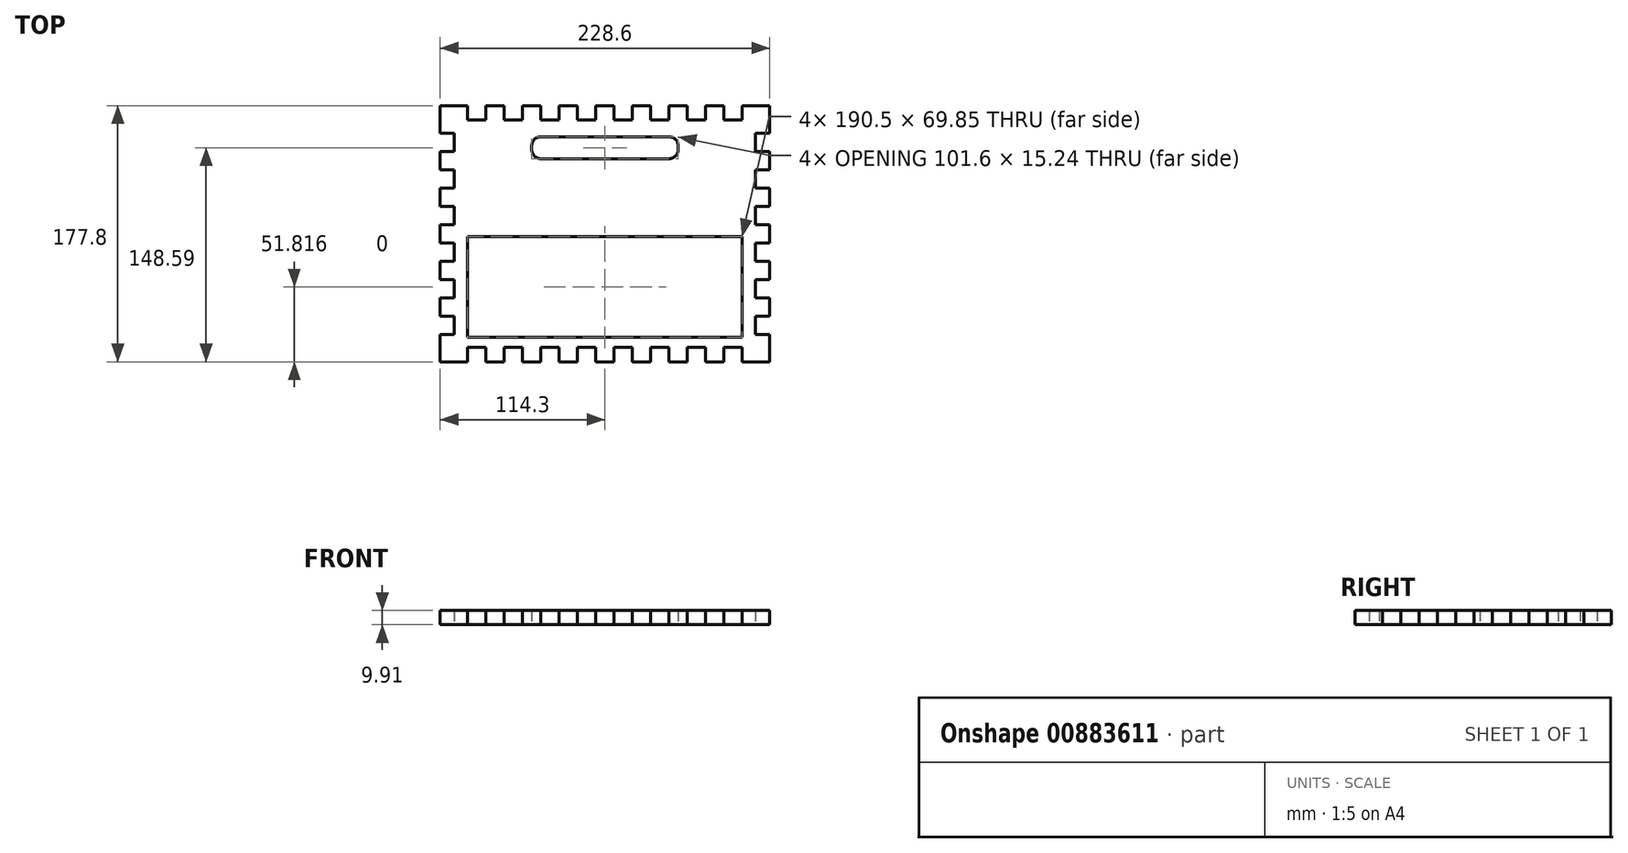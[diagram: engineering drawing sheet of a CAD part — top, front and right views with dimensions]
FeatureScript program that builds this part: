
annotation { "Feature Type Name" : "Feature", "Feature Type Description" : "" }
export const myFeature = defineFeature(function(context is Context, id is Id, definition is map)
    precondition{}
    {
        {
            var Q0;
            Q0=qCreatedBy(makeId("Top.planeOp"),FACE);
            var sketch = newSketch(context, id + "F0", { "sketchPlane" : qUnion([Q0])});
            skLineSegment(sketch, "E0.bottom", {"start": v(0, 0) * mm, "end": v(19.05, 0) * mm});
            skLineSegment(sketch, "E0.left", {"start": v(0, 0) * mm, "end": v(0, -19.05) * mm});
            skLineSegment(sketch, "E1", {"start": v(19.05, 0) * mm, "end": v(19.05, -9.9) * mm});
            skLineSegment(sketch, "E2", {"start": v(19.05, -9.9) * mm, "end": v(31.75, -9.9) * mm});
            skLineSegment(sketch, "E3", {"start": v(31.75, -9.9) * mm, "end": v(31.75, 0) * mm});
            skLineSegment(sketch, "E4", {"start": v(31.75, 0) * mm, "end": v(44.45, 0) * mm});
            skLineSegment(sketch, "E5", {"start": v(44.45, 0) * mm, "end": v(44.45, -9.9) * mm});
            skLineSegment(sketch, "E6", {"start": v(44.45, -9.9) * mm, "end": v(57.15, -9.9) * mm});
            skLineSegment(sketch, "E7", {"start": v(57.15, -9.9) * mm, "end": v(57.15, 0) * mm});
            skLineSegment(sketch, "E8", {"start": v(57.15, 0) * mm, "end": v(69.85, 0) * mm});
            skLineSegment(sketch, "E9", {"start": v(69.85, 0) * mm, "end": v(69.85, -9.9) * mm});
            skLineSegment(sketch, "E10", {"start": v(69.85, -9.9) * mm, "end": v(82.55, -9.9) * mm});
            skLineSegment(sketch, "E11", {"start": v(82.55, -9.9) * mm, "end": v(82.55, 0) * mm});
            skLineSegment(sketch, "E12.trimOffspring", {"start": v(82.55, 0) * mm, "end": v(95.25, 0) * mm});
            skLineSegment(sketch, "E13", {"start": v(95.25, 0) * mm, "end": v(95.25, -9.9) * mm});
            skLineSegment(sketch, "E14", {"start": v(95.25, -9.9) * mm, "end": v(107.95, -9.9) * mm});
            skLineSegment(sketch, "E15", {"start": v(107.95, -9.9) * mm, "end": v(107.95, 0) * mm});
            skLineSegment(sketch, "E16", {"start": v(107.95, 0) * mm, "end": v(120.65, 0) * mm});
            skLineSegment(sketch, "E17", {"start": v(120.65, 0) * mm, "end": v(120.65, -9.9) * mm});
            skLineSegment(sketch, "E18", {"start": v(120.65, -9.9) * mm, "end": v(133.35, -9.9) * mm});
            skLineSegment(sketch, "E19", {"start": v(133.35, -9.9) * mm, "end": v(133.35, 0) * mm});
            skLineSegment(sketch, "E20.trimOffspring", {"start": v(133.35, 0) * mm, "end": v(146.05, 0) * mm});
            skLineSegment(sketch, "E21", {"start": v(146.05, 0) * mm, "end": v(146.05, -9.9) * mm});
            skLineSegment(sketch, "E22", {"start": v(146.05, -9.9) * mm, "end": v(158.75, -9.9) * mm});
            skLineSegment(sketch, "E23", {"start": v(158.75, -9.9) * mm, "end": v(158.75, 0) * mm});
            skLineSegment(sketch, "E24", {"start": v(158.75, 0) * mm, "end": v(171.45, 0) * mm});
            skLineSegment(sketch, "E25", {"start": v(171.45, 0) * mm, "end": v(171.45, -9.9) * mm});
            skLineSegment(sketch, "E26", {"start": v(171.45, -9.9) * mm, "end": v(184.15, -9.9) * mm});
            skLineSegment(sketch, "E27", {"start": v(184.15, -9.9) * mm, "end": v(184.15, 0) * mm});
            skLineSegment(sketch, "E28", {"start": v(184.15, 0) * mm, "end": v(196.85, 0) * mm});
            skLineSegment(sketch, "E29", {"start": v(196.85, 0) * mm, "end": v(196.85, -9.9) * mm});
            skLineSegment(sketch, "E30", {"start": v(196.85, -9.9) * mm, "end": v(209.55, -9.9) * mm});
            skLineSegment(sketch, "E31", {"start": v(209.55, -9.9) * mm, "end": v(209.55, 0) * mm});
            skLineSegment(sketch, "E32.trimOffspring", {"start": v(209.55, 0) * mm, "end": v(228.6, 0) * mm});
            skLineSegment(sketch, "E33", {"start": v(0, -19.05) * mm, "end": v(9.9, -19.05) * mm});
            skLineSegment(sketch, "E34", {"start": v(9.9, -19.05) * mm, "end": v(9.9, -31.75) * mm});
            skLineSegment(sketch, "E35", {"start": v(9.9, -31.75) * mm, "end": v(0, -31.75) * mm});
            skLineSegment(sketch, "E36", {"start": v(0, -31.75) * mm, "end": v(0, -44.45) * mm});
            skLineSegment(sketch, "E37", {"start": v(0, -44.45) * mm, "end": v(9.9, -44.45) * mm});
            skLineSegment(sketch, "E38", {"start": v(9.9, -44.45) * mm, "end": v(9.9, -57.15) * mm});
            skLineSegment(sketch, "E39", {"start": v(9.9, -57.15) * mm, "end": v(0, -57.15) * mm});
            skLineSegment(sketch, "E40", {"start": v(0, -57.15) * mm, "end": v(0, -69.85) * mm});
            skLineSegment(sketch, "E41", {"start": v(0, -69.85) * mm, "end": v(9.9, -69.85) * mm});
            skLineSegment(sketch, "E42", {"start": v(9.9, -69.85) * mm, "end": v(9.9, -82.55) * mm});
            skLineSegment(sketch, "E43", {"start": v(9.9, -82.55) * mm, "end": v(0, -82.55) * mm});
            skLineSegment(sketch, "E44.trimOffspring", {"start": v(0, -82.55) * mm, "end": v(0, -95.25) * mm});
            skLineSegment(sketch, "E45", {"start": v(0, -95.25) * mm, "end": v(9.9, -95.25) * mm});
            skLineSegment(sketch, "E46", {"start": v(9.9, -95.25) * mm, "end": v(9.9, -107.95) * mm});
            skLineSegment(sketch, "E47", {"start": v(9.9, -107.95) * mm, "end": v(0, -107.95) * mm});
            skLineSegment(sketch, "E48.trimOffspring", {"start": v(0, -107.95) * mm, "end": v(0, -120.65) * mm});
            skLineSegment(sketch, "E49", {"start": v(0, -120.65) * mm, "end": v(9.9, -120.65) * mm});
            skLineSegment(sketch, "E50", {"start": v(9.9, -120.65) * mm, "end": v(9.9, -133.35) * mm});
            skLineSegment(sketch, "E51", {"start": v(9.9, -133.35) * mm, "end": v(0, -133.35) * mm});
            skLineSegment(sketch, "E52", {"start": v(0, -133.35) * mm, "end": v(0, -146.05) * mm});
            skLineSegment(sketch, "E53", {"start": v(0, -146.05) * mm, "end": v(9.9, -146.05) * mm});
            skLineSegment(sketch, "E54", {"start": v(9.9, -146.05) * mm, "end": v(9.9, -158.75) * mm});
            skLineSegment(sketch, "E55", {"start": v(9.9, -158.75) * mm, "end": v(0, -158.75) * mm});
            skLineSegment(sketch, "E56.trimOffspring", {"start": v(0, -158.75) * mm, "end": v(0, -177.8) * mm});
            skLineSegment(sketch, "E57", {"start": v(114.3, 0) * mm, "end": v(114.3, 0) * mm});
            skLineSegment(sketch, "E58", {"start": v(0, -88.9) * mm, "end": v(0, -88.9) * mm});
            skLineSegment(sketch, "E59.MirrorCS", {"start": v(228.6, -146.05) * mm, "end": v(218.7, -146.05) * mm});
            skLineSegment(sketch, "E60.MirrorCS", {"start": v(218.7, -107.95) * mm, "end": v(228.6, -107.95) * mm});
            skLineSegment(sketch, "E61.MirrorCS", {"start": v(228.6, -19.05) * mm, "end": v(218.7, -19.05) * mm});
            skLineSegment(sketch, "E62.MirrorCS", {"start": v(218.7, -57.15) * mm, "end": v(228.6, -57.15) * mm});
            skLineSegment(sketch, "E63.MirrorCS", {"start": v(218.7, -82.55) * mm, "end": v(228.6, -82.55) * mm});
            skLineSegment(sketch, "E64.MirrorCS", {"start": v(218.7, -31.75) * mm, "end": v(228.6, -31.75) * mm});
            skLineSegment(sketch, "E65.MirrorCS", {"start": v(218.7, -133.35) * mm, "end": v(228.6, -133.35) * mm});
            skLineSegment(sketch, "E66.MirrorCS", {"start": v(228.6, -82.55) * mm, "end": v(228.6, -95.25) * mm});
            skLineSegment(sketch, "E67.MirrorCS", {"start": v(228.6, -95.25) * mm, "end": v(218.7, -95.25) * mm});
            skLineSegment(sketch, "E68.MirrorCS", {"start": v(218.7, -158.75) * mm, "end": v(228.6, -158.75) * mm});
            skLineSegment(sketch, "E69.MirrorCS", {"start": v(228.6, -44.45) * mm, "end": v(218.7, -44.45) * mm});
            skLineSegment(sketch, "E70.MirrorCS", {"start": v(228.6, -69.85) * mm, "end": v(218.7, -69.85) * mm});
            skLineSegment(sketch, "E71.MirrorCS", {"start": v(228.6, -120.65) * mm, "end": v(218.7, -120.65) * mm});
            skLineSegment(sketch, "E72.MirrorCS", {"start": v(228.6, -31.75) * mm, "end": v(228.6, -44.45) * mm});
            skLineSegment(sketch, "E73.MirrorCS", {"start": v(228.6, -133.35) * mm, "end": v(228.6, -146.05) * mm});
            skLineSegment(sketch, "E74.MirrorCS", {"start": v(228.6, -57.15) * mm, "end": v(228.6, -69.85) * mm});
            skLineSegment(sketch, "E75.MirrorCS", {"start": v(228.6, 0) * mm, "end": v(228.6, -19.05) * mm});
            skLineSegment(sketch, "E76.MirrorCS", {"start": v(228.6, -107.95) * mm, "end": v(228.6, -120.65) * mm});
            skLineSegment(sketch, "E77.MirrorCS", {"start": v(228.6, 0) * mm, "end": v(209.55, 0) * mm});
            skLineSegment(sketch, "E78.MirrorCS", {"start": v(218.7, -19.05) * mm, "end": v(218.7, -31.75) * mm});
            skLineSegment(sketch, "E79.MirrorCS", {"start": v(218.7, -120.65) * mm, "end": v(218.7, -133.35) * mm});
            skLineSegment(sketch, "E80.MirrorCS", {"start": v(218.7, -44.45) * mm, "end": v(218.7, -57.15) * mm});
            skLineSegment(sketch, "E81.MirrorCS", {"start": v(218.7, -69.85) * mm, "end": v(218.7, -82.55) * mm});
            skLineSegment(sketch, "E82.MirrorCS", {"start": v(209.55, 0) * mm, "end": v(209.55, -9.9) * mm});
            skLineSegment(sketch, "E83.MirrorCS", {"start": v(218.7, -146.05) * mm, "end": v(218.7, -158.75) * mm});
            skLineSegment(sketch, "E84.MirrorCS", {"start": v(218.7, -95.25) * mm, "end": v(218.7, -107.95) * mm});
            skLineSegment(sketch, "E85.MirrorCS", {"start": v(228.6, -158.75) * mm, "end": v(228.6, -177.8) * mm});
            skLineSegment(sketch, "E86.MirrorCS", {"start": v(107.95, -177.8) * mm, "end": v(120.65, -177.8) * mm});
            skLineSegment(sketch, "E87.MirrorCS", {"start": v(209.55, -177.8) * mm, "end": v(209.55, -167.9) * mm});
            skLineSegment(sketch, "E88.MirrorCS", {"start": v(209.55, -167.9) * mm, "end": v(209.55, -177.8) * mm});
            skLineSegment(sketch, "E89.MirrorCS", {"start": v(133.35, -167.9) * mm, "end": v(133.35, -177.8) * mm});
            skLineSegment(sketch, "E90.MirrorCS", {"start": v(120.65, -177.8) * mm, "end": v(120.65, -167.9) * mm});
            skLineSegment(sketch, "E91.MirrorCS", {"start": v(19.05, -177.8) * mm, "end": v(19.05, -167.9) * mm});
            skLineSegment(sketch, "E92.MirrorCS", {"start": v(171.45, -177.8) * mm, "end": v(171.45, -167.9) * mm});
            skLineSegment(sketch, "E93.MirrorCS", {"start": v(107.95, -167.9) * mm, "end": v(107.95, -177.8) * mm});
            skLineSegment(sketch, "E94.MirrorCS", {"start": v(82.55, -167.9) * mm, "end": v(82.55, -177.8) * mm});
            skLineSegment(sketch, "E95.MirrorCS", {"start": v(196.85, -177.8) * mm, "end": v(196.85, -167.9) * mm});
            skLineSegment(sketch, "E96.MirrorCS", {"start": v(31.75, -167.9) * mm, "end": v(31.75, -177.8) * mm});
            skLineSegment(sketch, "E97.MirrorCS", {"start": v(158.75, -167.9) * mm, "end": v(158.75, -177.8) * mm});
            skLineSegment(sketch, "E98.MirrorCS", {"start": v(184.15, -167.9) * mm, "end": v(184.15, -177.8) * mm});
            skLineSegment(sketch, "E99.MirrorCS", {"start": v(57.15, -167.9) * mm, "end": v(57.15, -177.8) * mm});
            skLineSegment(sketch, "E100.MirrorCS", {"start": v(146.05, -177.8) * mm, "end": v(146.05, -167.9) * mm});
            skLineSegment(sketch, "E101.MirrorCS", {"start": v(95.25, -177.8) * mm, "end": v(95.25, -167.9) * mm});
            skLineSegment(sketch, "E102.MirrorCS", {"start": v(44.45, -177.8) * mm, "end": v(44.45, -167.9) * mm});
            skLineSegment(sketch, "E103.MirrorCS", {"start": v(69.85, -177.8) * mm, "end": v(69.85, -167.9) * mm});
            skLineSegment(sketch, "E104.MirrorCS", {"start": v(158.75, -177.8) * mm, "end": v(171.45, -177.8) * mm});
            skLineSegment(sketch, "E105.MirrorCS", {"start": v(82.55, -177.8) * mm, "end": v(95.25, -177.8) * mm});
            skLineSegment(sketch, "E106.MirrorCS", {"start": v(133.35, -177.8) * mm, "end": v(146.05, -177.8) * mm});
            skLineSegment(sketch, "E107.MirrorCS", {"start": v(31.75, -177.8) * mm, "end": v(44.45, -177.8) * mm});
            skLineSegment(sketch, "E108.MirrorCS", {"start": v(184.15, -177.8) * mm, "end": v(196.85, -177.8) * mm});
            skLineSegment(sketch, "E109.MirrorCS", {"start": v(57.15, -177.8) * mm, "end": v(69.85, -177.8) * mm});
            skLineSegment(sketch, "E110.MirrorCS", {"start": v(69.85, -167.9) * mm, "end": v(82.55, -167.9) * mm});
            skLineSegment(sketch, "E111.MirrorCS", {"start": v(120.65, -167.9) * mm, "end": v(133.35, -167.9) * mm});
            skLineSegment(sketch, "E112.MirrorCS", {"start": v(196.85, -167.9) * mm, "end": v(209.55, -167.9) * mm});
            skLineSegment(sketch, "E113.MirrorCS", {"start": v(19.05, -167.9) * mm, "end": v(31.75, -167.9) * mm});
            skLineSegment(sketch, "E114.MirrorCS", {"start": v(171.45, -167.9) * mm, "end": v(184.15, -167.9) * mm});
            skLineSegment(sketch, "E115.MirrorCS", {"start": v(44.45, -167.9) * mm, "end": v(57.15, -167.9) * mm});
            skLineSegment(sketch, "E116.MirrorCS", {"start": v(146.05, -167.9) * mm, "end": v(158.75, -167.9) * mm});
            skLineSegment(sketch, "E117.MirrorCS", {"start": v(95.25, -167.9) * mm, "end": v(107.95, -167.9) * mm});
            skLineSegment(sketch, "E118.MirrorCS", {"start": v(228.6, -177.8) * mm, "end": v(209.55, -177.8) * mm});
            skLineSegment(sketch, "E119.MirrorCS", {"start": v(0, -177.8) * mm, "end": v(19.05, -177.8) * mm});
            skLineSegment(sketch, "E120.bottom", {"start": v(19.05, -91.06) * mm, "end": v(209.55, -91.06) * mm});
            skLineSegment(sketch, "E120.top", {"start": v(19.05, -160.9) * mm, "end": v(209.55, -160.9) * mm});
            skLineSegment(sketch, "E120.left", {"start": v(19.05, -91.06) * mm, "end": v(19.05, -160.9) * mm});
            skLineSegment(sketch, "E120.right", {"start": v(209.55, -91.06) * mm, "end": v(209.55, -160.9) * mm});
            skLineSegment(sketch, "E121.bottom", {"start": v(69.85, -21.59) * mm, "end": v(158.75, -21.59) * mm});
            skLineSegment(sketch, "E121.top", {"start": v(69.85, -36.83) * mm, "end": v(158.75, -36.83) * mm});
            skLineSegment(sketch, "E121.left", {"start": v(63.5, -27.94) * mm, "end": v(63.5, -30.48) * mm});
            skLineSegment(sketch, "E121.right", {"start": v(165.1, -27.94) * mm, "end": v(165.1, -30.48) * mm});
            skLineSegment(sketch, "E122", {"start": v(114.3, -21.59) * mm, "end": v(114.3, 0) * mm, "construction": true});
            skPoint(sketch, "E123.visualSharp", {"position": v(63.5, -21.59) * mm});
            skArc(sketch, "E123.filletArc", {"start": v(69.85, -21.59) * mm, "mid": v(65.36, -23.45) * mm, "end": v(63.5, -27.94) * mm});
            skPoint(sketch, "E124.visualSharp", {"position": v(165.1, -21.59) * mm});
            skArc(sketch, "E124.filletArc", {"start": v(165.1, -27.94) * mm, "mid": v(163.24, -23.45) * mm, "end": v(158.75, -21.59) * mm});
            skPoint(sketch, "E125.visualSharp", {"position": v(165.1, -36.83) * mm});
            skArc(sketch, "E125.filletArc", {"start": v(158.75, -36.83) * mm, "mid": v(163.24, -34.97) * mm, "end": v(165.1, -30.48) * mm});
            skPoint(sketch, "E126.visualSharp", {"position": v(63.5, -36.83) * mm});
            skArc(sketch, "E126.filletArc", {"start": v(63.5, -30.48) * mm, "mid": v(65.36, -34.97) * mm, "end": v(69.85, -36.83) * mm});
            skSolve(sketch);
        }
        {
            var Q0;
            Q0=makeQuery(id+"F0.imprint","IMPRINT",FACE,{"disambiguationData":[TD([[makeQuery(id+"F0.imprint","IMPRINT",EDGE,{"derivedFrom":sQuery(id+"F0.wireOp",EDGE,"E0.bottom")}),-1.0]])]});
            extrude(context, id + "F1", {"entities" : qUnion([Q0]), "depth" : 9.9 * mm, "offsetDistance" : 25.4 * mm});
        }
        {
            var Q0;
            Q0=makeQuery(id+"F0.imprint","IMPRINT",FACE,{"disambiguationData":[TD([[makeQuery(id+"F0.imprint","IMPRINT",EDGE,{"derivedFrom":sQuery(id+"F0.wireOp",EDGE,"E39")}),1.0]])]});
            extrude(context, id + "F2", {"entities" : qUnion([Q0]), "depth" : 9.9 * mm, "offsetDistance" : 25.4 * mm});
        }
    });
